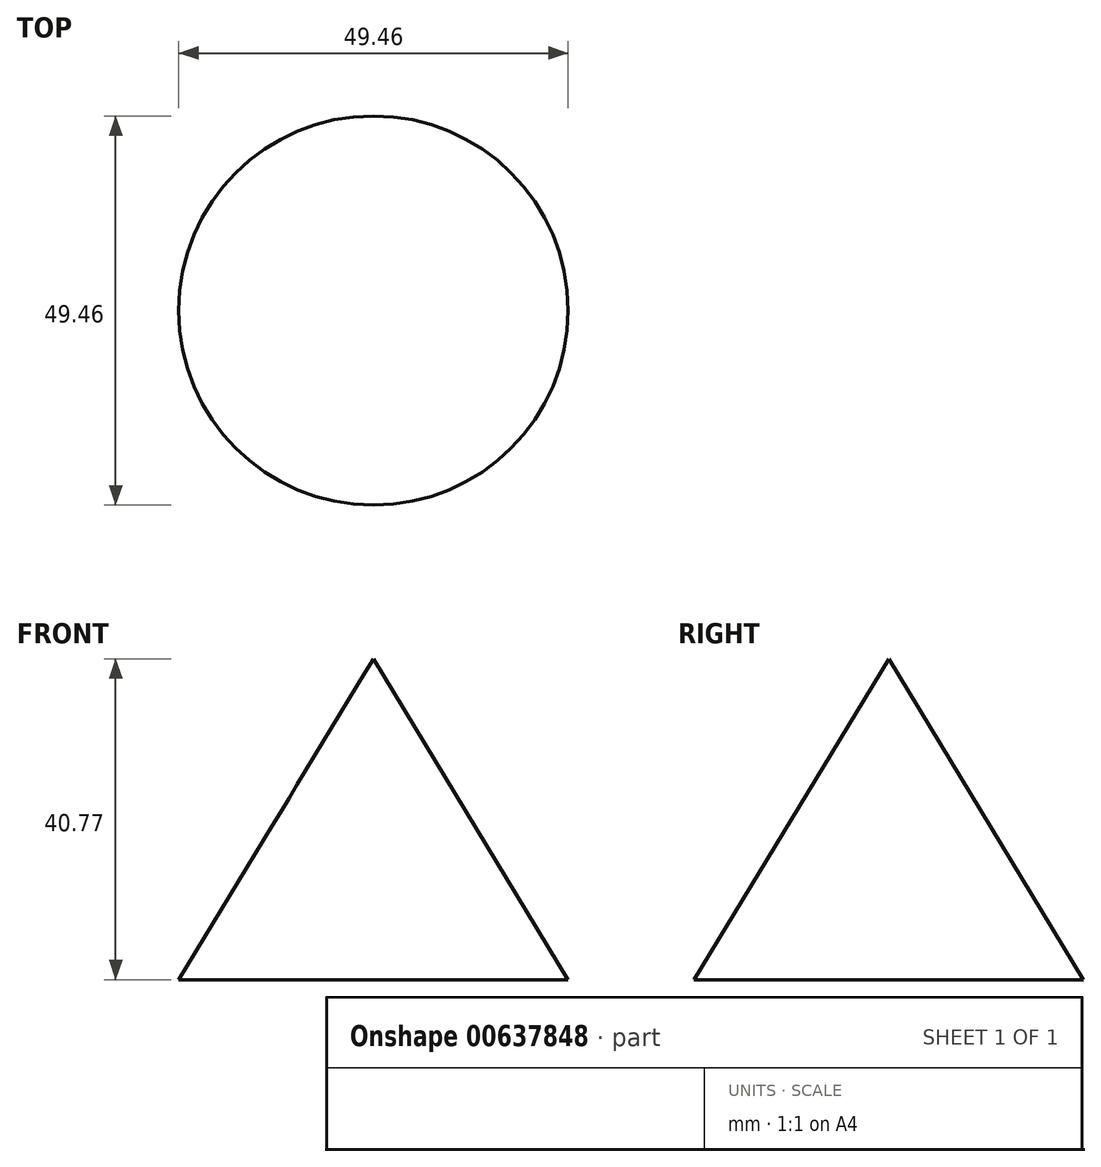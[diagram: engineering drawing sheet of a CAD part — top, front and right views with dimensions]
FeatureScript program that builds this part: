
annotation { "Feature Type Name" : "Feature", "Feature Type Description" : "" }
export const myFeature = defineFeature(function(context is Context, id is Id, definition is map)
    precondition{}
    {
        {
            var Q0;
            Q0=qCreatedBy(makeId("Front.planeOp"),FACE);
            var sketch = newSketch(context, id + "F0", { "sketchPlane" : qUnion([Q0])});
            skLineSegment(sketch, "E0", {"start": v(0, 0) * mm, "end": v(0, 40.77) * mm});
            skLineSegment(sketch, "E1", {"start": v(0, 40.77) * mm, "end": v(-24.73, 0) * mm});
            skLineSegment(sketch, "E2", {"start": v(-24.73, 0) * mm, "end": v(0, 0) * mm});
            skSolve(sketch);
        }
        {
            var Q0;
            Q0=makeQuery(id+"F0.imprint","IMPRINT",FACE,{"disambiguationData":[TD([[makeQuery(id+"F0.imprint","IMPRINT",EDGE,{"derivedFrom":sQuery(id+"F0.wireOp",EDGE,"E0")}),1.0]])]});
            var Q1;
            Q1=sQuery(id+"F0.wireOp",EDGE,"E0");
            revolve(context, id + "F1", {"entities" : qUnion([Q0]), "axis" : qUnion([Q1]), "revolveType" : RevolveType.FULL});
        }
    });
